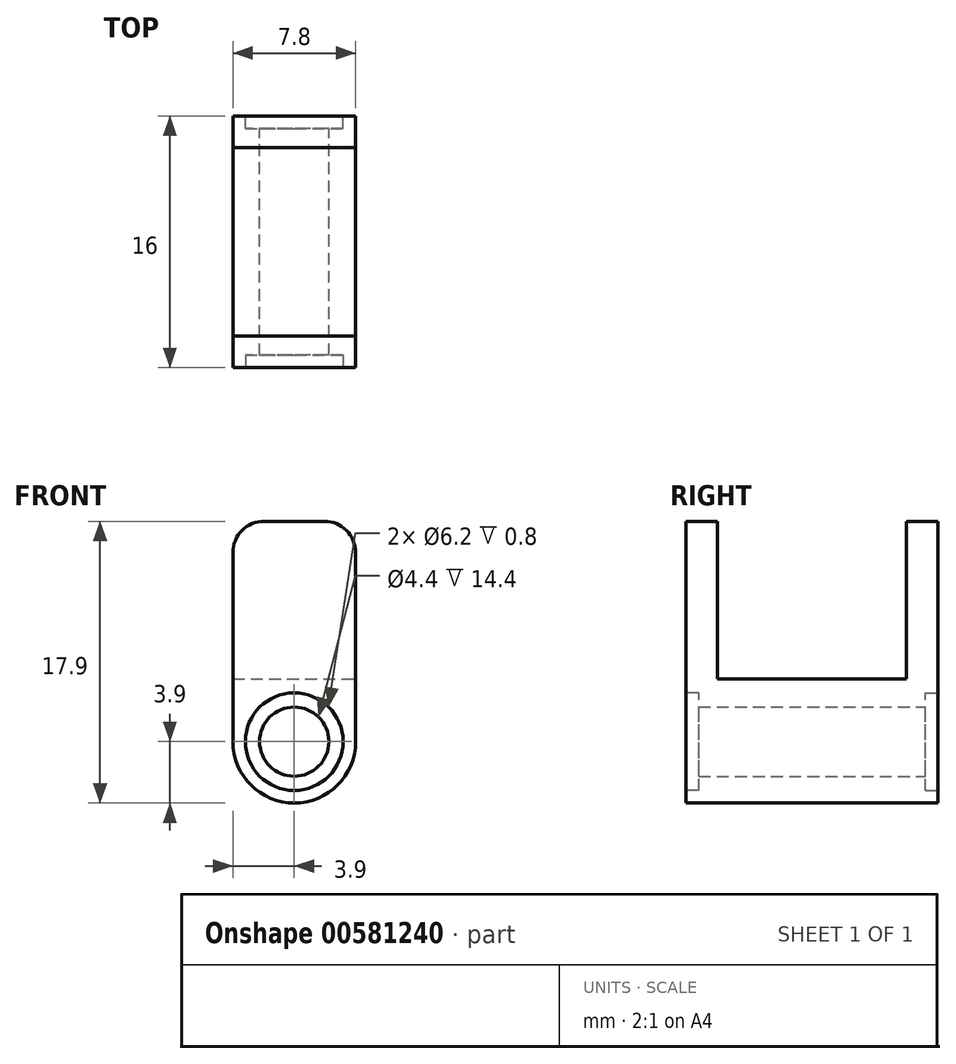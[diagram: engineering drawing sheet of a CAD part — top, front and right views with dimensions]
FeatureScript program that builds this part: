
annotation { "Feature Type Name" : "Feature", "Feature Type Description" : "" }
export const myFeature = defineFeature(function(context is Context, id is Id, definition is map)
    precondition{}
    {
        {
            var Q0;
            Q0=qCreatedBy(makeId("Top.planeOp"),FACE);
            var sketch = newSketch(context, id + "F0", { "sketchPlane" : qUnion([Q0])});
            skLineSegment(sketch, "E0.bottom", {"start": v(-3.9, 6) * mm, "end": v(3.9, 6) * mm});
            skLineSegment(sketch, "E0.top", {"start": v(-3.9, -6) * mm, "end": v(3.9, -6) * mm});
            skLineSegment(sketch, "E0.left", {"start": v(-6, 3.9) * mm, "end": v(-6, -3.9) * mm});
            skLineSegment(sketch, "E0.right", {"start": v(6, 3.9) * mm, "end": v(6, -3.9) * mm});
            skLineSegment(sketch, "E1", {"start": v(-6, 6) * mm, "end": v(6, -6) * mm, "construction": true});
            skLineSegment(sketch, "E2", {"start": v(-6, -6) * mm, "end": v(6, 6) * mm, "construction": true});
            skLineSegment(sketch, "E3", {"start": v(-6, 3.9) * mm, "end": v(-3.9, 6) * mm});
            skLineSegment(sketch, "E4", {"start": v(6, 3.9) * mm, "end": v(3.9, 6) * mm});
            skLineSegment(sketch, "E5", {"start": v(3.9, -6) * mm, "end": v(6, -3.9) * mm});
            skLineSegment(sketch, "E6", {"start": v(-6, -3.9) * mm, "end": v(-3.9, -6) * mm});
            skSolve(sketch);
        }
        {
            var Q0;
            Q0=makeQuery(id+"F0.imprint","IMPRINT",FACE,{"disambiguationData":[TD([[makeQuery(id+"F0.imprint","IMPRINT",EDGE,{"derivedFrom":sQuery(id+"F0.wireOp",EDGE,"E0.bottom")}),-1.0]])]});
            var Q1;
            Q1 = qConstructionFilter(qBodyType(qCreatedBy(id + "F0" ,EDGE), BodyType.WIRE), ConstructionObject.NO);
            extrude(context, id + "F1", {"entities" : qUnion([Q0]), "bodyType" : ExtendedToolBodyType.SURFACE, "surfaceEntities" : qUnion([Q1]), "depth" : 10 * mm, "offsetDistance" : 25 * mm});
        }
        {
            var Q0;
            Q0=qCreatedBy(makeId("Front.planeOp"),FACE);
            var sketch = newSketch(context, id + "F2", { "sketchPlane" : qUnion([Q0])});
            skCircle(sketch, "E7", {"center": v(0, -4) * mm, "radius": 2.2 * mm});
            skLineSegment(sketch, "E8.bottom", {"start": v(-3.9, 10) * mm, "end": v(3.9, 10) * mm});
            skLineSegment(sketch, "E8.left", {"start": v(-3.9, 10) * mm, "end": v(-3.9, -4) * mm});
            skLineSegment(sketch, "E8.right", {"start": v(3.9, 10) * mm, "end": v(3.9, -4) * mm});
            skArc(sketch, "E9", {"start": v(-3.9, -4) * mm, "mid": v(0, -7.9) * mm, "end": v(3.9, -4) * mm});
            skCircle(sketch, "E10", {"center": v(0, -4) * mm, "radius": 3.1 * mm});
            skSolve(sketch);
        }
        {
            var Q0;
            Q0=qCreatedBy(makeId("Right.planeOp"),FACE);
            var sketch = newSketch(context, id + "F3", { "sketchPlane" : qUnion([Q0])});
            skLineSegment(sketch, "E11.0", {"start": v(6, 0) * mm, "end": v(6, 10) * mm});
            skLineSegment(sketch, "E12.0", {"start": v(-6, 0) * mm, "end": v(-6, 10) * mm});
            skLineSegment(sketch, "E13", {"start": v(6, 0) * mm, "end": v(-6, 0) * mm});
            skLineSegment(sketch, "E14", {"start": v(6, 10) * mm, "end": v(-6, 10) * mm});
            skSolve(sketch);
        }
        {
            var Q0;
            Q0 = qSketchRegion(id + "F2", true);
            var Q1;
            Q1=makeQuery(id+"F2.imprint","IMPRINT",FACE,{"disambiguationData":[TD([[makeQuery(id+"F2.imprint","IMPRINT",EDGE,{"derivedFrom":sQuery(id+"F2.wireOp",EDGE,"E7")}),-1.0]])]});
            extrude(context, id + "F4", {"entities" : qUnion([Q0, Q1]), "depth" : 16 * mm, "offsetDistance" : 25 * mm, "symmetric" : true});
        }
        {
            var Q0;
            Q0 = qSketchRegion(id + "F3", true);
            extrude(context, id + "F5", {"entities" : qUnion([Q0]), "operationType" : NewBodyOperationType.REMOVE, "oppositeDirection" : true, "depth" : 25 * mm, "offsetDistance" : 25 * mm, "symmetric" : true});
        }
        {
            var Q0;
            {var subQ0=sQuery(id+"F2.wireOp",EDGE,"E8.left");var subQ1=sQuery(id+"F2.wireOp",EDGE,"E8.bottom");Q0=makeQuery(id+"F5.boolean.opBoolean","SPLIT",EDGE,{"disambiguationData":[TD([makeQuery(id+"F5.opExtrude","SWEPT_FACE",FACE,{"disambiguationData":[OSD([sQuery(id+"F3.wireOp",EDGE,"E12.0")])]})])],"derivedFrom":makeQuery(id+"F4.opExtrude","SWEPT_EDGE",EDGE,{"disambiguationData":[OSD([subQ1,subQ0])]})});}
            var Q1;
            {var subQ0=sQuery(id+"F2.wireOp",EDGE,"E8.right");var subQ1=sQuery(id+"F2.wireOp",EDGE,"E8.bottom");Q1=makeQuery(id+"F5.boolean.opBoolean","SPLIT",EDGE,{"disambiguationData":[TD([makeQuery(id+"F5.opExtrude","SWEPT_FACE",FACE,{"disambiguationData":[OSD([sQuery(id+"F3.wireOp",EDGE,"E12.0")])]})])],"derivedFrom":makeQuery(id+"F4.opExtrude","SWEPT_EDGE",EDGE,{"disambiguationData":[OSD([subQ1,subQ0])]})});}
            var Q2;
            {var subQ0=sQuery(id+"F2.wireOp",EDGE,"E8.right");var subQ1=sQuery(id+"F2.wireOp",EDGE,"E8.bottom");Q2=makeQuery(id+"F5.boolean.opBoolean","SPLIT",EDGE,{"disambiguationData":[TD([makeQuery(id+"F5.opExtrude","SWEPT_FACE",FACE,{"disambiguationData":[OSD([sQuery(id+"F3.wireOp",EDGE,"E11.0")])]})])],"derivedFrom":makeQuery(id+"F4.opExtrude","SWEPT_EDGE",EDGE,{"disambiguationData":[OSD([subQ1,subQ0])]})});}
            var Q3;
            {var subQ0=sQuery(id+"F2.wireOp",EDGE,"E8.left");var subQ1=sQuery(id+"F2.wireOp",EDGE,"E8.bottom");Q3=makeQuery(id+"F5.boolean.opBoolean","SPLIT",EDGE,{"disambiguationData":[TD([makeQuery(id+"F5.opExtrude","SWEPT_FACE",FACE,{"disambiguationData":[OSD([sQuery(id+"F3.wireOp",EDGE,"E11.0")])]})])],"derivedFrom":makeQuery(id+"F4.opExtrude","SWEPT_EDGE",EDGE,{"disambiguationData":[OSD([subQ1,subQ0])]})});}
            fillet(context, id + "F6", {"entities" : qUnion([Q0, Q1, Q2, Q3]), "tangentPropagation" : true, "radius" : 2 * mm, "defaultsChanged" : true, "vertexSettings" : [], "allowEdgeOverflow" : false});
        }
        {
            var Q0;
            Q0=makeQuery(id+"F2.imprint","IMPRINT",FACE,{"disambiguationData":[TD([[makeQuery(id+"F2.imprint","IMPRINT",EDGE,{"derivedFrom":sQuery(id+"F2.wireOp",EDGE,"E7")}),-1.0]])]});
            extrude(context, id + "F7", {"entities" : qUnion([Q0]), "depth" : 0.8 * mm, "offsetDistance" : 25 * mm});
        }
        {
            var Q0;
            Q0=makeQuery(id+"F7.opExtrude","SWEPT_BODY",BODY,{"disambiguationData":[OSD([sQuery(id+"F2.wireOp",EDGE,"E7"),sQuery(id+"F2.wireOp",EDGE,"E10")])]});
            var Q1;
            Q1=qCreatedBy(makeId("Front.planeOp"),FACE);
            transform(context, id + "F8", {"entities" : qUnion([Q0]), "transformType" : TransformType.TRANSLATION_DISTANCE, "transformDirection" : qUnion([Q1]), "distance" : 8 * mm, "oppositeDirection" : true, "makeCopy" : false});
        }
        {
            var Q0;
            Q0=makeQuery(id+"F7.opExtrude","SWEPT_BODY",BODY,{"disambiguationData":[OSD([sQuery(id+"F2.wireOp",EDGE,"E7"),sQuery(id+"F2.wireOp",EDGE,"E10")])]});
            var Q1;
            Q1=qCreatedBy(makeId("Front.planeOp"),FACE);
            mirror(context, id + "F9", {"entities" : qUnion([Q0]), "mirrorPlane" : qUnion([Q1])});
        }
        {
            var Q0;
            Q0=makeQuery(id+"F7.opExtrude","SWEPT_BODY",BODY,{"disambiguationData":[OSD([sQuery(id+"F2.wireOp",EDGE,"E7"),sQuery(id+"F2.wireOp",EDGE,"E10")])]});
            var Q1;
            Q1=makeQuery(id+"F9.opPattern","COPY",BODY,{"derivedFrom":makeQuery(id+"F7.opExtrude","SWEPT_BODY",BODY,{"disambiguationData":[OSD([sQuery(id+"F2.wireOp",EDGE,"E7"),sQuery(id+"F2.wireOp",EDGE,"E10")])]}),"instanceName":"1"});
            var Q2;
            Q2=makeQuery(id+"F4.opExtrude","SWEPT_BODY",BODY,{"disambiguationData":[OSD([sQuery(id+"F2.wireOp",EDGE,"E7"),sQuery(id+"F2.wireOp",EDGE,"E8.bottom"),sQuery(id+"F2.wireOp",EDGE,"E8.left"),sQuery(id+"F2.wireOp",EDGE,"E8.right"),sQuery(id+"F2.wireOp",EDGE,"E9")])]});
            booleanBodies(context, id + "F10", {"operationType" : BooleanOperationType.SUBTRACTION, "tools" : qUnion([Q0, Q1]), "targets" : qUnion([Q2])});
        }
    });
